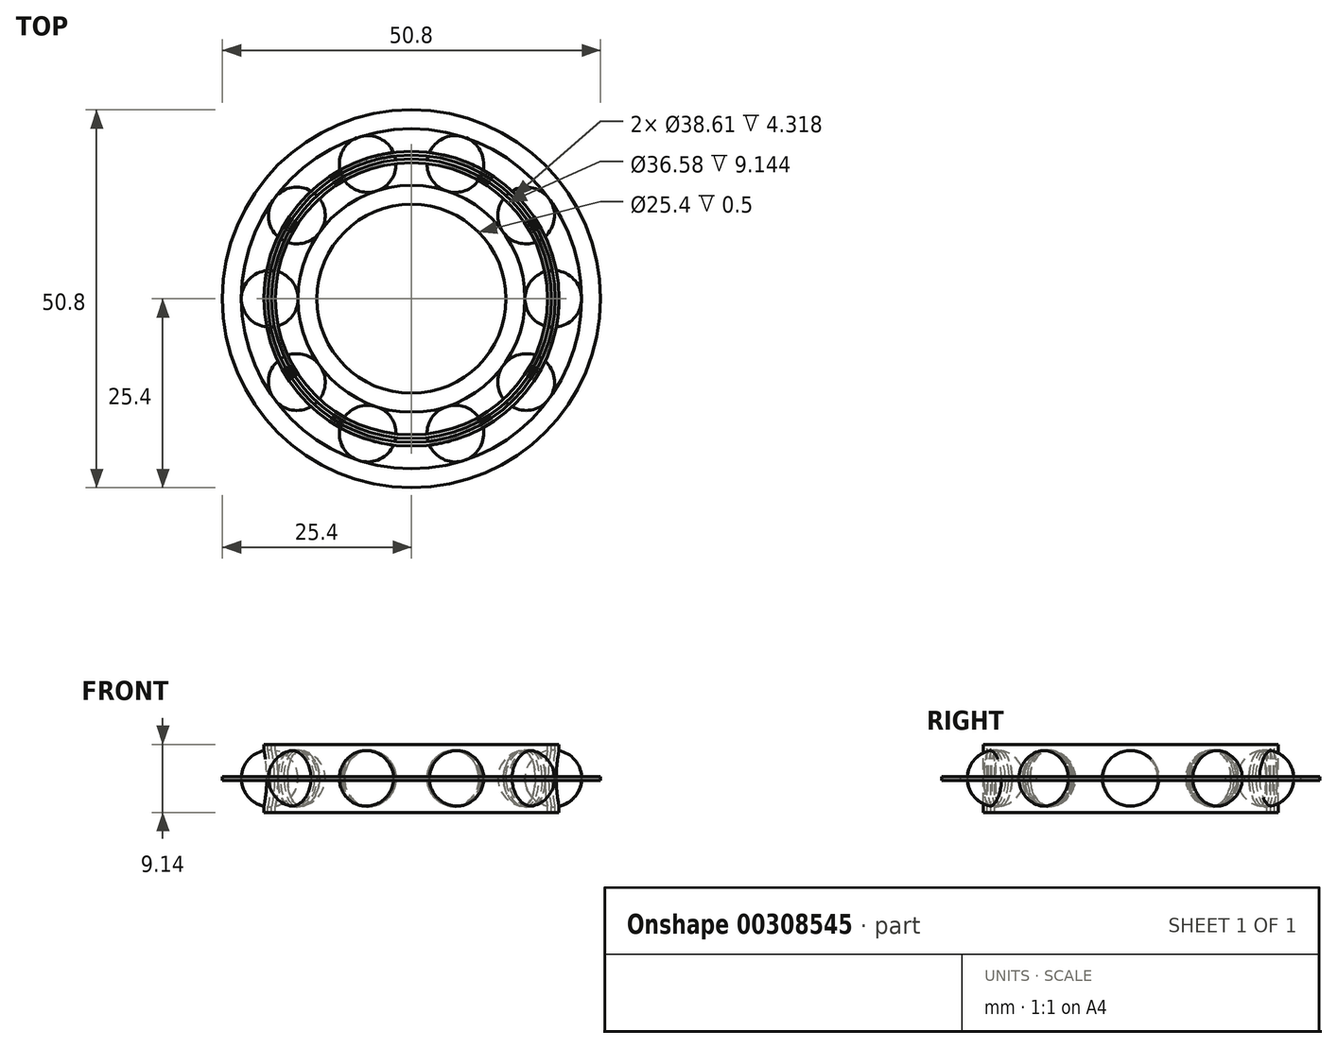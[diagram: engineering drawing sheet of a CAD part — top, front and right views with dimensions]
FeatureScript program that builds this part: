
annotation { "Feature Type Name" : "Feature", "Feature Type Description" : "" }
export const myFeature = defineFeature(function(context is Context, id is Id, definition is map)
    precondition{}
    {
        {
            assignVariable(context, id + "F0", {"name" : "ball_count", "anyValue" : 0});
        }
        {
            assignVariable(context, id + "F1", {"name" : "id_in", "anyValue" : 1});
        }
        {
            assignVariable(context, id + "F2", {"name" : "od_in", "anyValue" : 2});
        }
        {
            assignVariable(context, id + "F3", {"name" : "len_in", "anyValue" : .5});
        }
        {
            assignVariable(context, id + "F4", {"name" : "bMetric", "anyValue" : 0});
        }
        {
            assignVariable(context, id + "F5", {"name" : "id_mm", "anyValue" : 25.4});
        }
        {
            assignVariable(context, id + "F6", {"name" : "od_mm", "anyValue" : 50.8});
        }
        {
            assignVariable(context, id + "F7", {"name" : "len_mm", "anyValue" : 12.7});
        }
        {
            assignVariable(context, id + "F8", {"name" : "id", "anyValue" : [getVariable(context, 'id_in'), getVariable(context, 'id_mm') / 25.4][getVariable(context, 'bMetric')]});
        }
        {
            assignVariable(context, id + "F9", {"name" : "od", "anyValue" : [getVariable(context, 'od_in'), getVariable(context, 'od_mm') / 25.4][getVariable(context, 'bMetric')]});
        }
        {
            assignVariable(context, id + "F10", {"name" : "len", "anyValue" : [getVariable(context, 'len_in'), getVariable(context, 'len_mm') / 25.4][getVariable(context, 'bMetric')]});
        }
        {
            assignVariable(context, id + "F11", {"name" : "radial_thk", "anyValue" : (getVariable(context, 'od') - getVariable(context, 'id')) / 2});
        }
        {
            assignVariable(context, id + "F12", {"name" : "ball_dia", "anyValue" : .6 * getVariable(context, 'radial_thk')});
        }
        {
            assignVariable(context, id + "F13", {"name" : "mean_dia", "anyValue" : (getVariable(context, 'od') + getVariable(context, 'id')) / 2});
        }
        {
            assignVariable(context, id + "F14", {"name" : "ball_calc", "anyValue" : ((PI * getVariable(context, 'mean_dia')) / (1.5 * getVariable(context, 'ball_dia')))});
        }
        {
            assignVariable(context, id + "F15", {"name" : "N", "anyValue" : [floor(getVariable(context, 'ball_calc')), getVariable(context, 'ball_count')][getVariable(context, 'ball_count') % (getVariable(context, 'ball_count') - 1)]});
        }
        {
            var Q0;
            Q0=qCreatedBy(makeId("Top.planeOp"),FACE);
            var sketch = newSketch(context, id + "F16", { "sketchPlane" : qUnion([Q0])});
            skCircle(sketch, "E0", {"center": v(0, 0) * mm, "radius": 12.7 * mm});
            skCircle(sketch, "E1", {"center": v(0, 0) * mm, "radius": 25.4 * mm});
            skSolve(sketch);
        }
        {
            var Q0;
            Q0=qSketchRegion(id+"F16",true);
            extrude(context, id + "F17", {"entities" : qUnion([Q0]), "depth" : (getVariable(context, 'len')) * mm, "symmetric" : true});
        }
        {
            var Q0;
            Q0=qCreatedBy(makeId("Top.planeOp"),FACE);
            var sketch = newSketch(context, id + "F18", { "sketchPlane" : qUnion([Q0])});
            skCircle(sketch, "E2", {"center": v(0, 0) * mm, "radius": 12.7 * mm});
            skCircle(sketch, "E3", {"center": v(0, 0) * mm, "radius": 16.76 * mm});
            skCircle(sketch, "E4", {"center": v(0, 0) * mm, "radius": 21.34 * mm});
            skCircle(sketch, "E5", {"center": v(0, 0) * mm, "radius": 25.4 * mm});
            skCircle(sketch, "E6", {"center": v(0, 0) * mm, "radius": 19.05 * mm, "construction": true});
            skLineSegment(sketch, "E7", {"start": v(16.76, 0) * mm, "end": v(21.34, 0) * mm, "construction": true});
            skPoint(sketch, "E8", {"position": v(19.05, 0) * mm});
            skLineSegment(sketch, "E9", {"start": v(-25.4, 0) * mm, "end": v(-12.7, 0) * mm, "construction": true});
            skPoint(sketch, "E10", {"position": v(-19.05, 0) * mm});
            skPoint(sketch, "E11", {"position": v(12.7, 0) * mm});
            skPoint(sketch, "E12", {"position": v(25.4, 0) * mm});
            skSolve(sketch);
        }
        {
            var Q0;
            Q0=makeQuery(id+"F18.imprint","IMPRINT",FACE,{"disambiguationData":[TD([[makeQuery(id+"F18.imprint","IMPRINT",EDGE,{"derivedFrom":sQuery(id+"F18.wireOp",EDGE,"E4")}),-1.0]])]});
            var Q1;
            Q1=makeQuery(id+"F18.imprint","IMPRINT",FACE,{"disambiguationData":[TD([[makeQuery(id+"F18.imprint","IMPRINT",EDGE,{"derivedFrom":sQuery(id+"F18.wireOp",EDGE,"E2")}),-1.0]])]});
            extrude(context, id + "F19", {"entities" : qUnion([Q0, Q1]), "depth" : (getVariable(context, 'len')) * mm, "symmetric" : true});
        }
        {
            var Q0;
            Q0=makeQuery(id+"F19.opExtrude","CAP_EDGE",EDGE,{"disambiguationData":[OSD([sQuery(id+"F18.wireOp",EDGE,"E5")])],"isStart":false});
            var Q1;
            Q1=makeQuery(id+"F19.opExtrude","CAP_EDGE",EDGE,{"disambiguationData":[OSD([sQuery(id+"F18.wireOp",EDGE,"E5")])],"isStart":true});
            fillet(context, id + "F20", {"entities" : qUnion([Q0, Q1]), "radius" : (getVariable(context, 'len') / 10) * mm, "tangentPropagation" : true, "allowEdgeOverflow" : false});
        }
        {
            var Q0;
            Q0=makeQuery(id+"F19.opExtrude","CAP_EDGE",EDGE,{"disambiguationData":[OSD([sQuery(id+"F18.wireOp",EDGE,"E2")])],"isStart":true});
            var Q1;
            Q1=makeQuery(id+"F19.opExtrude","CAP_EDGE",EDGE,{"disambiguationData":[OSD([sQuery(id+"F18.wireOp",EDGE,"E2")])],"isStart":false});
            fillet(context, id + "F21", {"entities" : qUnion([Q0, Q1]), "radius" : (getVariable(context, 'len') / 15) * mm, "tangentPropagation" : true, "allowEdgeOverflow" : false});
        }
        {
            var Q0;
            Q0=qCreatedBy(makeId("Front.planeOp"),FACE);
            var sketch = newSketch(context, id + "F22", { "sketchPlane" : qUnion([Q0])});
            skLineSegment(sketch, "E13", {"start": v(0, 6.35) * mm, "end": v(0, -6.35) * mm, "construction": true});
            skCircle(sketch, "E14", {"center": v(19.05, 0) * mm, "radius": 3.81 * mm});
            skSolve(sketch);
        }
        {
            var Q0;
            Q0=qSketchRegion(id+"F22",true);
            var Q1;
            Q1=sQuery(id+"F22.wireOp",EDGE,"E13");
            revolve(context, id + "F23", {"operationType" : NewBodyOperationType.REMOVE, "entities" : qUnion([Q0]), "axis" : qUnion([Q1]), "revolveType" : RevolveType.FULL, "oppositeDirection" : true});
        }
        {
            var Q0;
            Q0=qCreatedBy(makeId("Front.planeOp"),FACE);
            var sketch = newSketch(context, id + "F24", { "sketchPlane" : qUnion([Q0])});
            skLineSegment(sketch, "E15.bottom", {"start": v(18.8, -4.57) * mm, "end": v(18.29, -4.57) * mm});
            skLineSegment(sketch, "E15.top", {"start": v(18.8, 4.57) * mm, "end": v(18.29, 4.57) * mm});
            skLineSegment(sketch, "E15.left", {"start": v(18.8, -4.57) * mm, "end": v(18.8, -0.25) * mm});
            skLineSegment(sketch, "E15.right", {"start": v(18.29, -4.57) * mm, "end": v(18.29, 4.57) * mm});
            skLineSegment(sketch, "E16.bottom", {"start": v(19.3, 4.57) * mm, "end": v(19.81, 4.57) * mm});
            skLineSegment(sketch, "E16.top", {"start": v(19.3, -4.57) * mm, "end": v(19.81, -4.57) * mm});
            skLineSegment(sketch, "E16.left", {"start": v(19.3, 4.57) * mm, "end": v(19.3, 0.25) * mm});
            skLineSegment(sketch, "E16.right", {"start": v(19.81, 4.57) * mm, "end": v(19.81, -4.57) * mm});
            skLineSegment(sketch, "E17.bottom", {"start": v(19.3, -0.25) * mm, "end": v(18.8, -0.25) * mm});
            skLineSegment(sketch, "E17.top", {"start": v(19.3, 0.25) * mm, "end": v(18.8, 0.25) * mm});
            skPoint(sketch, "E17.middle", {"position": v(19.05, 0) * mm});
            skLineSegment(sketch, "E18.trimOffspring", {"start": v(18.8, 0.25) * mm, "end": v(18.8, 4.57) * mm});
            skLineSegment(sketch, "E19.trimOffspring", {"start": v(19.3, -0.25) * mm, "end": v(19.3, -4.57) * mm});
            skLineSegment(sketch, "E20", {"start": v(19.05, 0.25) * mm, "end": v(19.05, -0.25) * mm, "construction": true});
            skLineSegment(sketch, "E21", {"start": v(18.8, 0.25) * mm, "end": v(19.3, -0.25) * mm, "construction": true});
            skLineSegment(sketch, "E22", {"start": v(19.3, 0.25) * mm, "end": v(18.8, -0.25) * mm, "construction": true});
            skSolve(sketch);
        }
        {
            var Q0;
            Q0=qSketchRegion(id+"F24",true);
            var Q1;
            Q1=sQuery(id+"F22.wireOp",EDGE,"E13");
            revolve(context, id + "F25", {"entities" : qUnion([Q0]), "axis" : qUnion([Q1]), "revolveType" : RevolveType.FULL});
        }
        {
            var Q0;
            Q0=qCreatedBy(makeId("Front.planeOp"),FACE);
            var sketch = newSketch(context, id + "F26", { "sketchPlane" : qUnion([Q0])});
            skLineSegment(sketch, "E23", {"start": v(-6.35, 0) * mm, "end": v(6.35, 0) * mm, "construction": true});
            skLineSegment(sketch, "E24.0", {"start": v(15.24, 0) * mm, "end": v(15.24, 0) * mm});
            skArc(sketch, "E25", {"start": v(22.86, 0) * mm, "mid": v(19.05, 3.81) * mm, "end": v(15.24, 0) * mm});
            skLineSegment(sketch, "E26", {"start": v(15.24, 0) * mm, "end": v(22.86, 0) * mm});
            skSolve(sketch);
        }
        {
            var Q0;
            Q0=qSketchRegion(id+"F26",true);
            var Q1;
            Q1=sQuery(id+"F26.wireOp",EDGE,"E26");
            revolve(context, id + "F27", {"entities" : qUnion([Q0]), "axis" : qUnion([Q1]), "revolveType" : RevolveType.FULL});
        }
        {
            var Q0;
            Q0=makeQuery(id+"F27.opRevolve","SWEPT_BODY",BODY,{"disambiguationData":[OSD([sQuery(id+"F26.wireOp",EDGE,"E25"),sQuery(id+"F26.wireOp",EDGE,"E26")])]});
            var Q1;
            Q1=makeQuery(id+"F25.opRevolve","SWEPT_FACE",FACE,{"disambiguationData":[OSD([sQuery(id+"F24.wireOp",EDGE,"E15.right")])]});
            circularPattern(context, id + "F28", {"operationType" : NewBodyOperationType.ADD, "entities" : qUnion([Q0]), "axis" : qUnion([Q1]), "angle" : 360 * degree, "instanceCount" : getVariable(context, 'N'), "equalSpace" : true});
        }
    });
